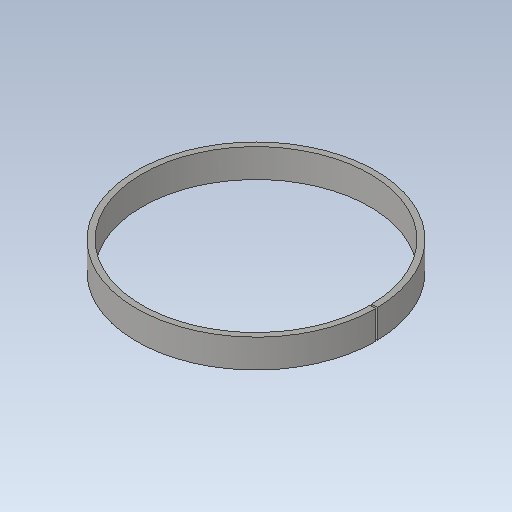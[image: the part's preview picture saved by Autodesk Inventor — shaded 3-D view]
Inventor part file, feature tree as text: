
AUTODESK INVENTOR PART (.ipt)
format: ipt  version: 2020.1 (Build 241239000, 239)  size: 147,456 bytes
history: native  units: mm
features: sketch x2, revolve x1, extrude x1, other x1
ambient origin geometry x8: Origin, YZ Plane, XZ Plane, XY Plane, X Axis, Y Axis, Z Axis, Center Point
bodies: Solid1 (feature_tree)
feature tree (5):
  revolve  "Revolution1"  [1 undecoded]
  extrude  "Extrusion1"  Depth=10.0mm
  sketch  "Sketch1"  dims[d0=5.0mm d1=200.0mm]
  sketch  "Sketch2"  dims[d2=25.0mm d3=62.65732mm d4=10.0mm d5=210.0mm d6=25.0mm d7=12.5mm d8=105.0mm d9=10.0mm d10=0.0mm]
  other  "Definition1"
note: 1 required parameter value undecoded (feature->parameter linkage not recoverable at this tier; creation-order binding heuristic only, values carry confidence <= 0.55)
